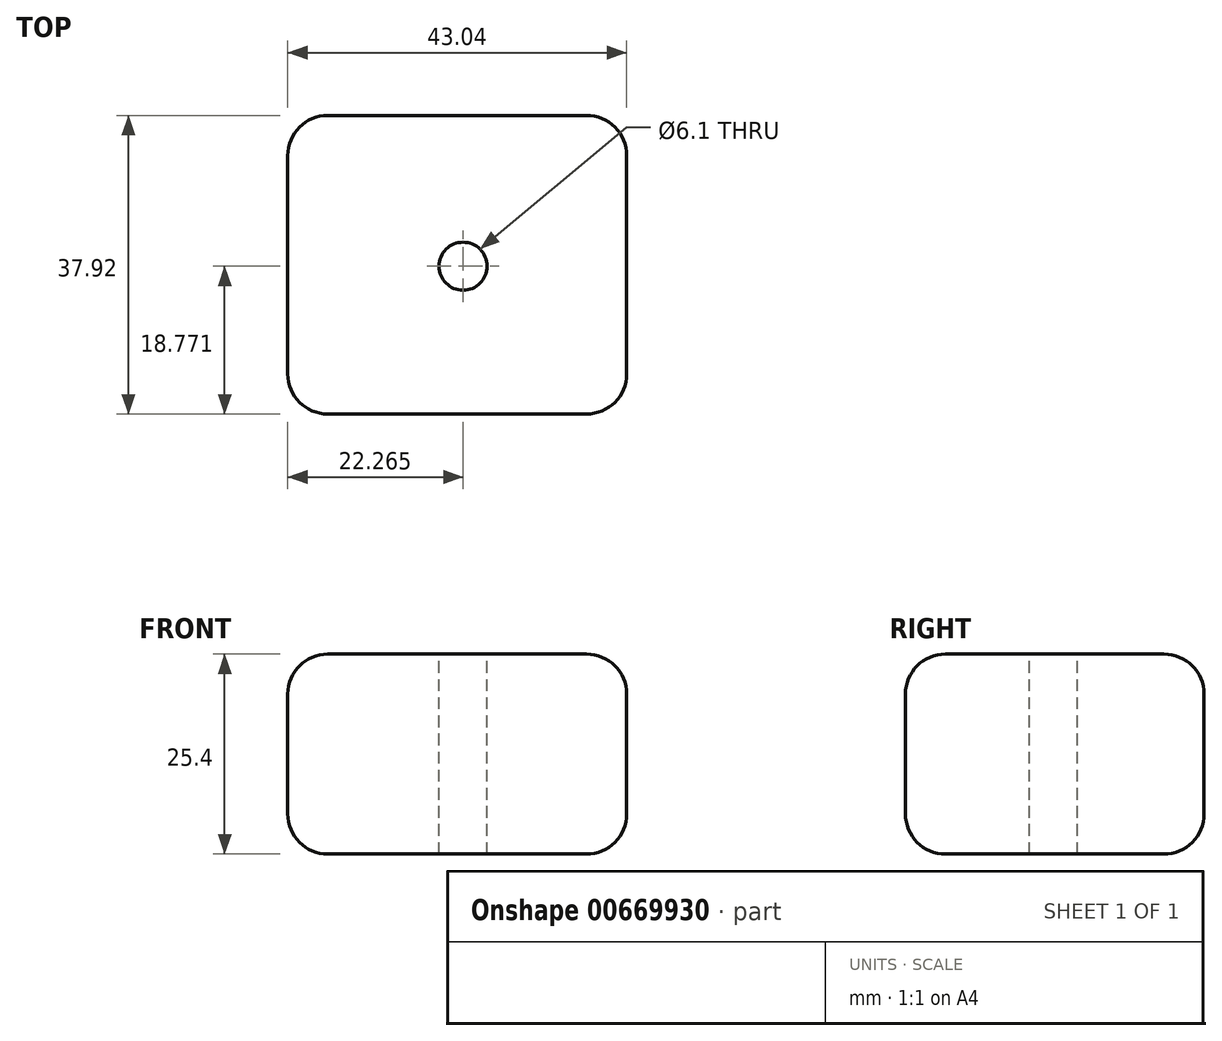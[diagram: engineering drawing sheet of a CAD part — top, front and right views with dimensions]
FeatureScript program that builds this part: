
annotation { "Feature Type Name" : "Feature", "Feature Type Description" : "" }
export const myFeature = defineFeature(function(context is Context, id is Id, definition is map)
    precondition{}
    {
        {
            var Q0;
            Q0=qCreatedBy(makeId("Top.planeOp"),FACE);
            var sketch = newSketch(context, id + "F0", { "sketchPlane" : qUnion([Q0])});
            skLineSegment(sketch, "E0", {"start": v(43.04, 0) * mm, "end": v(0, 0) * mm});
            skLineSegment(sketch, "E1", {"start": v(0, 0) * mm, "end": v(0, 37.92) * mm});
            skLineSegment(sketch, "E2", {"start": v(0, 37.92) * mm, "end": v(43.04, 37.92) * mm});
            skLineSegment(sketch, "E3", {"start": v(43.04, 37.92) * mm, "end": v(43.04, 0) * mm});
            skSolve(sketch);
        }
        {
            var Q0;
            Q0=makeQuery(id+"F0.imprint","IMPRINT",FACE,{"disambiguationData":[TD([[makeQuery(id+"F0.imprint","IMPRINT",EDGE,{"derivedFrom":sQuery(id+"F0.wireOp",EDGE,"E0")}),-1.0]])]});
            extrude(context, id + "F1", {"entities" : qUnion([Q0]), "depth" : 25.4 * mm, "offsetDistance" : 25.4 * mm});
        }
        {
            var Q0;
            Q0=makeQuery(id+"F1.opExtrude","CAP_EDGE",EDGE,{"disambiguationData":[OSD([sQuery(id+"F0.wireOp",EDGE,"E3")])],"isStart":true});
            var Q1;
            Q1=makeQuery(id+"F1.opExtrude","CAP_EDGE",EDGE,{"disambiguationData":[OSD([sQuery(id+"F0.wireOp",EDGE,"E2")])],"isStart":true});
            var Q2;
            Q2=makeQuery(id+"F1.opExtrude","CAP_EDGE",EDGE,{"disambiguationData":[OSD([sQuery(id+"F0.wireOp",EDGE,"E0")])],"isStart":true});
            var Q3;
            Q3=makeQuery(id+"F1.opExtrude","CAP_EDGE",EDGE,{"disambiguationData":[OSD([sQuery(id+"F0.wireOp",EDGE,"E1")])],"isStart":true});
            var Q4;
            Q4=makeQuery(id+"F1.opExtrude","CAP_EDGE",EDGE,{"disambiguationData":[OSD([sQuery(id+"F0.wireOp",EDGE,"E3")])],"isStart":false});
            var Q5;
            Q5=makeQuery(id+"F1.opExtrude","SWEPT_EDGE",EDGE,{"disambiguationData":[OSD([sQuery(id+"F0.wireOp",EDGE,"E2"),sQuery(id+"F0.wireOp",EDGE,"E3")])]});
            var Q6;
            Q6=makeQuery(id+"F1.opExtrude","SWEPT_EDGE",EDGE,{"disambiguationData":[OSD([sQuery(id+"F0.wireOp",EDGE,"E0"),sQuery(id+"F0.wireOp",EDGE,"E3")])]});
            var Q7;
            Q7=makeQuery(id+"F1.opExtrude","SWEPT_EDGE",EDGE,{"disambiguationData":[OSD([sQuery(id+"F0.wireOp",EDGE,"E0"),sQuery(id+"F0.wireOp",EDGE,"E1")])]});
            var Q8;
            Q8=makeQuery(id+"F1.opExtrude","SWEPT_EDGE",EDGE,{"disambiguationData":[OSD([sQuery(id+"F0.wireOp",EDGE,"E1"),sQuery(id+"F0.wireOp",EDGE,"E2")])]});
            var Q9;
            Q9=makeQuery(id+"F1.opExtrude","CAP_EDGE",EDGE,{"disambiguationData":[OSD([sQuery(id+"F0.wireOp",EDGE,"E2")])],"isStart":false});
            var Q10;
            Q10=makeQuery(id+"F1.opExtrude","CAP_EDGE",EDGE,{"disambiguationData":[OSD([sQuery(id+"F0.wireOp",EDGE,"E0")])],"isStart":false});
            var Q11;
            Q11=makeQuery(id+"F1.opExtrude","CAP_EDGE",EDGE,{"disambiguationData":[OSD([sQuery(id+"F0.wireOp",EDGE,"E1")])],"isStart":false});
            fillet(context, id + "F2", {"entities" : qUnion([Q0, Q1, Q2, Q3, Q4, Q5, Q6, Q7, Q8, Q9, Q10, Q11]), "radius" : 5.08 * mm, "tangentPropagation" : true, "allowEdgeOverflow" : false});
        }
        {
            var Q0;
            Q0=makeQuery(id+"F1.opExtrude","CAP_FACE",FACE,{"disambiguationData":[OSD([sQuery(id+"F0.wireOp",EDGE,"E0"),sQuery(id+"F0.wireOp",EDGE,"E1"),sQuery(id+"F0.wireOp",EDGE,"E2"),sQuery(id+"F0.wireOp",EDGE,"E3")])],"isStart":false});
            var sketch = newSketch(context, id + "F3", { "sketchPlane" : qUnion([Q0])});
            skCircle(sketch, "E4", {"center": v(33.84, 64.8) * mm, "radius": 0.35 * mm});
            skCircle(sketch, "E5", {"center": v(22.27, 18.77) * mm, "radius": 3.05 * mm});
            skSolve(sketch);
        }
        {
            var Q0;
            Q0=makeQuery(id+"F3.imprint","IMPRINT",FACE,{"disambiguationData":[TD([[makeQuery(id+"F3.imprint","IMPRINT",EDGE,{"derivedFrom":sQuery(id+"F3.wireOp",EDGE,"E5")}),1.0]])]});
            var Q1;
            Q1=sQuery(id+"F3.wireOp",EDGE,"E5");
            extrude(context, id + "F4", {"entities" : qUnion([Q0]), "operationType" : NewBodyOperationType.REMOVE, "surfaceEntities" : qUnion([Q1]), "oppositeDirection" : true, "depth" : 25.4 * mm, "offsetDistance" : 25.4 * mm});
        }
    });
